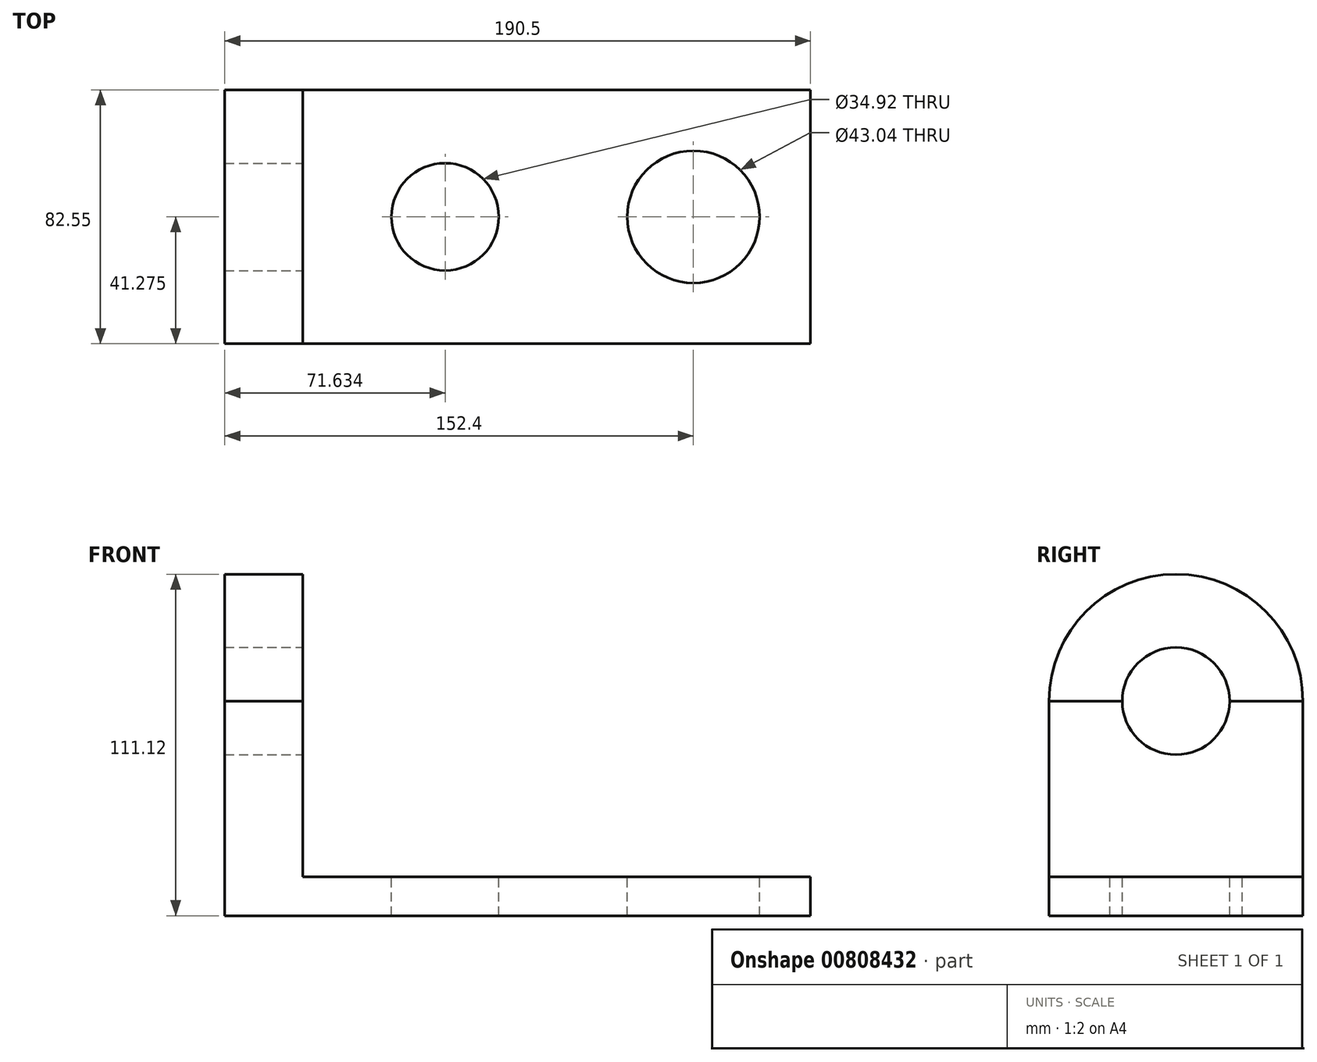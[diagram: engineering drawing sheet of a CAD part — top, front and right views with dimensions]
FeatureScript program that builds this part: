
annotation { "Feature Type Name" : "Feature", "Feature Type Description" : "" }
export const myFeature = defineFeature(function(context is Context, id is Id, definition is map)
    precondition{}
    {
        {
            var Q0;
            Q0=qCreatedBy(makeId("Front.planeOp"),FACE);
            var sketch = newSketch(context, id + "F0", { "sketchPlane" : qUnion([Q0])});
            skLineSegment(sketch, "E0", {"start": v(0, 0) * mm, "end": v(190.5, 0) * mm});
            skLineSegment(sketch, "E1", {"start": v(190.5, 0) * mm, "end": v(190.5, 12.7) * mm});
            skLineSegment(sketch, "E2", {"start": v(190.5, 12.7) * mm, "end": v(25.4, 12.7) * mm});
            skLineSegment(sketch, "E3", {"start": v(25.4, 12.7) * mm, "end": v(25.4, 69.85) * mm});
            skLineSegment(sketch, "E4", {"start": v(25.4, 69.85) * mm, "end": v(0, 69.85) * mm});
            skLineSegment(sketch, "E5", {"start": v(0, 69.85) * mm, "end": v(0, 0) * mm});
            skSolve(sketch);
        }
        {
            var Q0;
            Q0 = qSketchRegion(id + "F0", true);
            extrude(context, id + "F1", {"entities" : qUnion([Q0]), "depth" : 82.55 * mm, "offsetDistance" : 25.4 * mm});
        }
        {
            var Q0;
            Q0=makeQuery(id+"F1.opExtrude","SWEPT_FACE",FACE,{"disambiguationData":[OSD([sQuery(id+"F0.wireOp",EDGE,"E3")])]});
            var sketch = newSketch(context, id + "F2", { "sketchPlane" : qUnion([Q0])});
            skArc(sketch, "E6", {"start": v(0, 69.85) * mm, "mid": v(-41.28, 111.12) * mm, "end": v(-82.55, 69.85) * mm});
            skSolve(sketch);
        }
        {
            var Q0;
            Q0=makeQuery(id+"F2.imprint","IMPRINT",FACE,{"disambiguationData":[TD([[makeQuery(id+"F2.imprint","IMPRINT",EDGE,{"derivedFrom":sQuery(id+"F2.wireOp",EDGE,"E6")}),1.0]])]});
            extrude(context, id + "F3", {"entities" : qUnion([Q0]), "oppositeDirection" : true, "depth" : 25.4 * mm, "offsetDistance" : 25.4 * mm});
        }
        {
            var Q0;
            Q0=makeQuery(id+"F1.opExtrude","SWEPT_FACE",FACE,{"disambiguationData":[OSD([sQuery(id+"F0.wireOp",EDGE,"E2")])]});
            var sketch = newSketch(context, id + "F4", { "sketchPlane" : qUnion([Q0])});
            skLineSegment(sketch, "E7", {"start": v(190.5, -41.28) * mm, "end": v(152.4, -41.28) * mm, "construction": true});
            skCircle(sketch, "E8", {"center": v(152.4, -41.28) * mm, "radius": 21.52 * mm});
            skLineSegment(sketch, "E9", {"start": v(152.4, -41.28) * mm, "end": v(71.63, -41.28) * mm, "construction": true});
            skCircle(sketch, "E10", {"center": v(71.63, -41.28) * mm, "radius": 17.46 * mm});
            skSolve(sketch);
        }
        {
            var Q0;
            Q0 = qSketchRegion(id + "F4", true);
            var Q1;
            Q1=makeQuery(id+"F4.imprint","IMPRINT",FACE,{"disambiguationData":[TD([[makeQuery(id+"F4.imprint","IMPRINT",EDGE,{"derivedFrom":sQuery(id+"F4.wireOp",EDGE,"E10")}),1.0]])]});
            extrude(context, id + "F5", {"entities" : qUnion([Q0, Q1]), "operationType" : NewBodyOperationType.REMOVE, "oppositeDirection" : true, "depth" : 25.4 * mm, "offsetDistance" : 25.4 * mm});
        }
        {
            var Q0;
            Q0=makeQuery(id+"F1.opExtrude","SWEPT_FACE",FACE,{"disambiguationData":[OSD([sQuery(id+"F0.wireOp",EDGE,"E3")])]});
            var sketch = newSketch(context, id + "F6", { "sketchPlane" : qUnion([Q0])});
            skCircle(sketch, "E11", {"center": v(-41.28, 69.85) * mm, "radius": 17.46 * mm});
            skSolve(sketch);
        }
        {
            var Q0;
            {var subQ0=sQuery(id+"F6.wireOp",EDGE,"E11");var subQ1=makeQuery(id+"F1.opExtrude","SWEPT_EDGE",EDGE,{"disambiguationData":[OSD([sQuery(id+"F0.wireOp",EDGE,"E3"),sQuery(id+"F0.wireOp",EDGE,"E4")])]});var subQ2=makeQuery(id+"F6.imprint","INTERSECT",VERTEX,{"disambiguationData":[OD(0.0)],"derivedFrom":[subQ1,subQ0]});Q0=makeQuery(id+"F6.imprint","IMPRINT",FACE,{"disambiguationData":[TD([[makeQuery(id+"F6.imprint","IMPRINT",EDGE,{"disambiguationData":[TD([[subQ2,1.0]])],"derivedFrom":subQ0}),1.0]])]});}
            extrude(context, id + "F7", {"entities" : qUnion([Q0]), "operationType" : NewBodyOperationType.REMOVE, "oppositeDirection" : true, "depth" : 25.4 * mm, "offsetDistance" : 25.4 * mm});
        }
        {
            var Q0;
            Q0=makeQuery(id+"F3.opExtrude","CAP_FACE",FACE,{"disambiguationData":[OSD([sQuery(id+"F0.wireOp",EDGE,"E3"),sQuery(id+"F0.wireOp",EDGE,"E4"),sQuery(id+"F2.wireOp",EDGE,"E6")])],"isStart":true});
            var sketch = newSketch(context, id + "F8", { "sketchPlane" : qUnion([Q0])});
            skCircle(sketch, "E12", {"center": v(-41.28, 69.85) * mm, "radius": 17.46 * mm});
            skSolve(sketch);
        }
        {
            var Q0;
            {var subQ0=sQuery(id+"F8.wireOp",EDGE,"E12");var subQ1=makeQuery(id+"F3.opExtrude","CAP_EDGE",EDGE,{"disambiguationData":[OSD([sQuery(id+"F0.wireOp",EDGE,"E3"),sQuery(id+"F0.wireOp",EDGE,"E4")])],"isStart":true});var subQ2=makeQuery(id+"F8.imprint","INTERSECT",VERTEX,{"disambiguationData":[OD(0.0)],"derivedFrom":[subQ1,subQ0]});Q0=makeQuery(id+"F8.imprint","IMPRINT",FACE,{"disambiguationData":[TD([[makeQuery(id+"F8.imprint","IMPRINT",EDGE,{"disambiguationData":[TD([[subQ2,-1.0]])],"derivedFrom":subQ0}),1.0]])]});}
            extrude(context, id + "F9", {"entities" : qUnion([Q0]), "operationType" : NewBodyOperationType.REMOVE, "oppositeDirection" : true, "depth" : 25.4 * mm, "offsetDistance" : 25.4 * mm});
        }
    });
